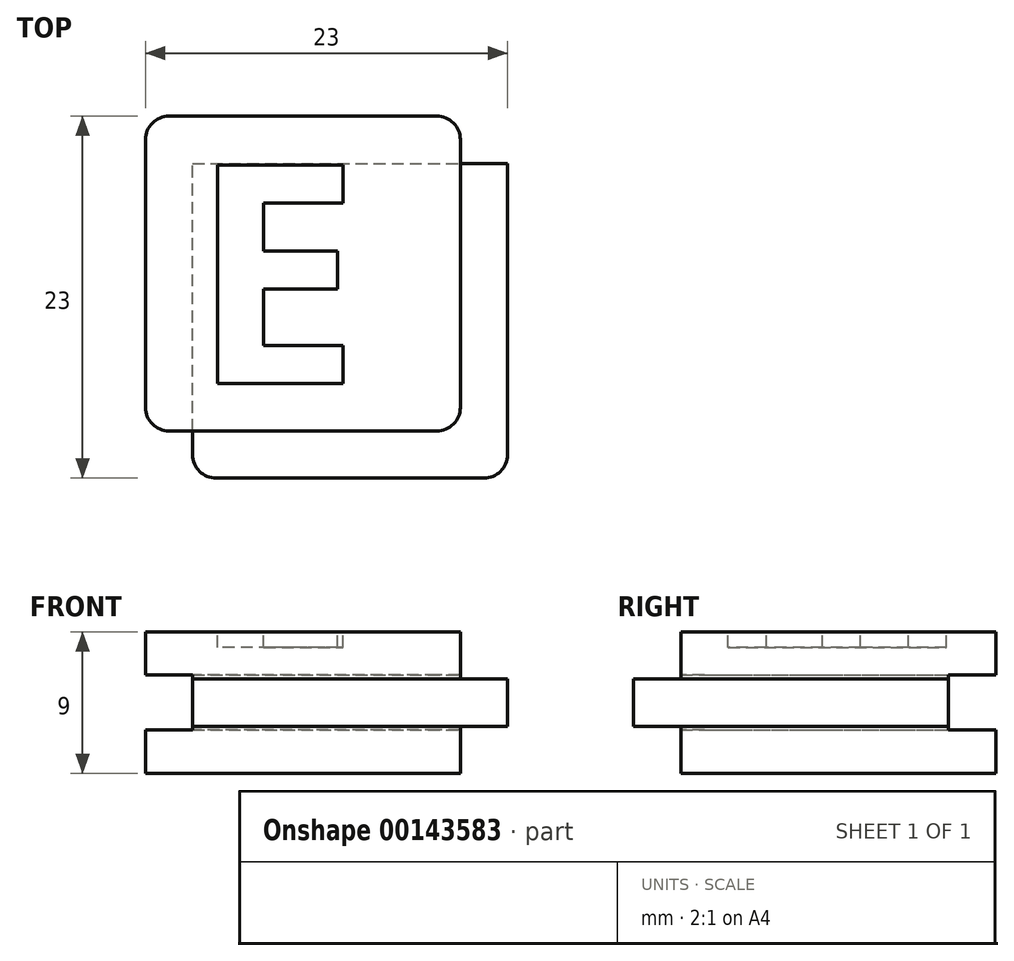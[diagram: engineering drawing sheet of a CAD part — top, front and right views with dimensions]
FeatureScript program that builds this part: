
annotation { "Feature Type Name" : "Feature", "Feature Type Description" : "" }
export const myFeature = defineFeature(function(context is Context, id is Id, definition is map)
    precondition{}
    {
        {
            var Q0;
            Q0=qCreatedBy(makeId("Front.planeOp"),FACE);
            var sketch = newSketch(context, id + "F0", { "sketchPlane" : qUnion([Q0])});
            skLineSegment(sketch, "E0.bottom", {"start": v(10, 4.5) * mm, "end": v(-10, 4.5) * mm});
            skLineSegment(sketch, "E0.top", {"start": v(10, -4.5) * mm, "end": v(-10, -4.5) * mm});
            skLineSegment(sketch, "E0.left", {"start": v(10, 4.5) * mm, "end": v(10, -4.5) * mm});
            skLineSegment(sketch, "E0.right", {"start": v(-10, 4.5) * mm, "end": v(-10, -4.5) * mm});
            skPoint(sketch, "E0.middle", {"position": v(0, 0) * mm});
            skLineSegment(sketch, "E1.bottom", {"start": v(13, 1.5) * mm, "end": v(7, 1.5) * mm});
            skLineSegment(sketch, "E1.top", {"start": v(13, -1.5) * mm, "end": v(7, -1.5) * mm});
            skLineSegment(sketch, "E1.left", {"start": v(13, 1.5) * mm, "end": v(13, -1.5) * mm});
            skLineSegment(sketch, "E1.right", {"start": v(7, 1.5) * mm, "end": v(7, -1.5) * mm});
            skPoint(sketch, "E1.middle", {"position": v(10, 0) * mm});
            skLineSegment(sketch, "E2.bottom", {"start": v(7, 1.5) * mm, "end": v(-7, 1.5) * mm});
            skLineSegment(sketch, "E2.top", {"start": v(7, -1.5) * mm, "end": v(-7, -1.5) * mm});
            skLineSegment(sketch, "E2.right", {"start": v(-7, 1.5) * mm, "end": v(-7, -1.5) * mm});
            skLineSegment(sketch, "E3.bottom", {"start": v(-7, -1.5) * mm, "end": v(-10, -1.5) * mm});
            skLineSegment(sketch, "E3.top", {"start": v(-7, 1.5) * mm, "end": v(-10, 1.5) * mm});
            skLineSegment(sketch, "E3.left", {"start": v(-7, -1.5) * mm, "end": v(-7, 1.5) * mm});
            skLineSegment(sketch, "E3.right", {"start": v(-10, -1.5) * mm, "end": v(-10, 1.5) * mm});
            skSolve(sketch);
        }
        {
            var Q0;
            {var subQ5=sQuery(id+"F0.wireOp",EDGE,"E0.bottom");Q0=makeQuery(id+"F0.imprint","IMPRINT",FACE,{"disambiguationData":[TD([[makeQuery(id+"F0.imprint","IMPRINT",EDGE,{"derivedFrom":subQ5}),1.0]])]});}
            var Q1;
            Q1=makeQuery(id+"F0.imprint","IMPRINT",FACE,{"disambiguationData":[TD([[makeQuery(id+"F0.imprint","IMPRINT",EDGE,{"derivedFrom":sQuery(id+"F0.wireOp",EDGE,"E2.bottom")}),1.0]])]});
            var Q2;
            {var subQ5=sQuery(id+"F0.wireOp",EDGE,"E1.left");Q2=makeQuery(id+"F0.imprint","IMPRINT",FACE,{"disambiguationData":[TD([[makeQuery(id+"F0.imprint","IMPRINT",EDGE,{"derivedFrom":subQ5}),-1.0]])]});}
            var Q3;
            {var subQ5=sQuery(id+"F0.wireOp",EDGE,"E1.right");Q3=makeQuery(id+"F0.imprint","IMPRINT",FACE,{"disambiguationData":[TD([[makeQuery(id+"F0.imprint","IMPRINT",EDGE,{"derivedFrom":subQ5}),1.0]])]});}
            var Q4;
            Q4=makeQuery(id+"F0.imprint","IMPRINT",FACE,{"disambiguationData":[TD([[makeQuery(id+"F0.imprint","IMPRINT",EDGE,{"derivedFrom":sQuery(id+"F0.wireOp",EDGE,"E3.bottom")}),-1.0]])]});
            var Q5;
            {var subQ5=sQuery(id+"F0.wireOp",EDGE,"E0.top");Q5=makeQuery(id+"F0.imprint","IMPRINT",FACE,{"disambiguationData":[TD([[makeQuery(id+"F0.imprint","IMPRINT",EDGE,{"derivedFrom":subQ5}),-1.0]])]});}
            extrude(context, id + "F1", {"entities" : qUnion([Q0, Q1, Q2, Q3, Q4, Q5]), "oppositeDirection" : true, "depth" : 20 * mm});
        }
        {
            var Q0;
            Q0=makeQuery(id+"F0.imprint","IMPRINT",FACE,{"disambiguationData":[TD([[makeQuery(id+"F0.imprint","IMPRINT",EDGE,{"derivedFrom":sQuery(id+"F0.wireOp",EDGE,"E3.bottom")}),-1.0]])]});
            var Q1;
            Q1=makeQuery(id+"F0.imprint","IMPRINT",FACE,{"disambiguationData":[TD([[makeQuery(id+"F0.imprint","IMPRINT",EDGE,{"derivedFrom":sQuery(id+"F0.wireOp",EDGE,"E2.bottom")}),1.0]])]});
            var Q2;
            {var subQ5=sQuery(id+"F0.wireOp",EDGE,"E1.right");Q2=makeQuery(id+"F0.imprint","IMPRINT",FACE,{"disambiguationData":[TD([[makeQuery(id+"F0.imprint","IMPRINT",EDGE,{"derivedFrom":subQ5}),1.0]])]});}
            var Q3;
            {var subQ5=sQuery(id+"F0.wireOp",EDGE,"E1.left");Q3=makeQuery(id+"F0.imprint","IMPRINT",FACE,{"disambiguationData":[TD([[makeQuery(id+"F0.imprint","IMPRINT",EDGE,{"derivedFrom":subQ5}),-1.0]])]});}
            extrude(context, id + "F2", {"entities" : qUnion([Q0, Q1, Q2, Q3]), "operationType" : NewBodyOperationType.ADD, "depth" : 3 * mm});
        }
        {
            var Q0;
            {var subQ0=sQuery(id+"F0.wireOp",EDGE,"E1.left");Q0=makeQuery(id+"F2.boolean.opBoolean","MERGE",FACE,{"derivedFrom":[makeQuery(id+"F1.opExtrude","SWEPT_FACE",FACE,{"disambiguationData":[OSD([subQ0])]}),makeQuery(id+"F2.opExtrude","SWEPT_FACE",FACE,{"disambiguationData":[OSD([subQ0])]})]});}
            var sketch = newSketch(context, id + "F3", { "sketchPlane" : qUnion([Q0])});
            skLineSegment(sketch, "E4.bottom", {"start": v(23, 1.75) * mm, "end": v(17, 1.75) * mm});
            skLineSegment(sketch, "E4.top", {"start": v(23, -1.75) * mm, "end": v(17, -1.75) * mm});
            skLineSegment(sketch, "E4.left", {"start": v(23, 1.75) * mm, "end": v(23, -1.75) * mm});
            skLineSegment(sketch, "E4.right", {"start": v(17, 1.75) * mm, "end": v(17, -1.75) * mm});
            skPoint(sketch, "E4.middle", {"position": v(20, 0) * mm});
            skSolve(sketch);
        }
        {
            var Q0;
            {var subQ1=sQuery(id+"F3.wireOp",EDGE,"E4.bottom");Q0=makeQuery(id+"F3.imprint","IMPRINT",FACE,{"disambiguationData":[TD([[makeQuery(id+"F3.imprint","IMPRINT",EDGE,{"derivedFrom":subQ1}),1.0]])]});}
            var Q1;
            {var subQ1=sQuery(id+"F0.wireOp",EDGE,"E1.left");var subQ8=makeQuery(id+"F1.opExtrude","CAP_EDGE",EDGE,{"disambiguationData":[OSD([subQ1])],"isStart":false});Q1=makeQuery(id+"F3.imprint","IMPRINT",FACE,{"disambiguationData":[TD([[makeQuery(id+"F3.imprint","IMPRINT",EDGE,{"derivedFrom":subQ8}),-1.0]])]});}
            extrude(context, id + "F4", {"entities" : qUnion([Q0, Q1]), "operationType" : NewBodyOperationType.REMOVE, "oppositeDirection" : true, "depth" : 100 * mm});
        }
        {
            var Q0;
            Q0=makeQuery(id+"F4.boolean.opBoolean","COPY",FACE,{"derivedFrom":makeQuery(id+"F4.opExtrude","SWEPT_FACE",FACE,{"disambiguationData":[OSD([sQuery(id+"F3.wireOp",EDGE,"E4.right")])]})});
            var sketch = newSketch(context, id + "F5", { "sketchPlane" : qUnion([Q0])});
            skLineSegment(sketch, "E5.bottom", {"start": v(13, 1.75) * mm, "end": v(7, 1.75) * mm});
            skLineSegment(sketch, "E5.top", {"start": v(13, -1.75) * mm, "end": v(7, -1.75) * mm});
            skLineSegment(sketch, "E5.left", {"start": v(13, 1.75) * mm, "end": v(13, -1.75) * mm});
            skLineSegment(sketch, "E5.right", {"start": v(7, 1.75) * mm, "end": v(7, -1.75) * mm});
            skPoint(sketch, "E5.middle", {"position": v(10, 0) * mm});
            skSolve(sketch);
        }
        {
            var Q0;
            {var subQ3=sQuery(id+"F5.wireOp",EDGE,"E5.left");Q0=makeQuery(id+"F5.imprint","IMPRINT",FACE,{"disambiguationData":[TD([[makeQuery(id+"F5.imprint","IMPRINT",EDGE,{"derivedFrom":subQ3}),-1.0]])]});}
            var Q1;
            {var subQ4=sQuery(id+"F5.wireOp",EDGE,"E5.right");Q1=makeQuery(id+"F5.imprint","IMPRINT",FACE,{"disambiguationData":[TD([[makeQuery(id+"F5.imprint","IMPRINT",EDGE,{"derivedFrom":subQ4}),1.0]])]});}
            extrude(context, id + "F6", {"entities" : qUnion([Q0, Q1]), "operationType" : NewBodyOperationType.REMOVE, "oppositeDirection" : true, "depth" : 100 * mm});
        }
        {
            var Q0;
            Q0=makeQuery(id+"F6.boolean.opBoolean","INTERSECT",EDGE,{"derivedFrom":[makeQuery(id+"F2.opExtrude","CAP_FACE",FACE,{"disambiguationData":[OSD([sQuery(id+"F0.wireOp",EDGE,"E1.bottom"),sQuery(id+"F0.wireOp",EDGE,"E1.top"),sQuery(id+"F0.wireOp",EDGE,"E1.left"),sQuery(id+"F0.wireOp",EDGE,"E2.bottom"),sQuery(id+"F0.wireOp",EDGE,"E2.top"),sQuery(id+"F0.wireOp",EDGE,"E3.bottom"),sQuery(id+"F0.wireOp",EDGE,"E3.top"),sQuery(id+"F0.wireOp",EDGE,"E3.right")])],"isStart":false}),makeQuery(id+"F6.opExtrude","SWEPT_FACE",FACE,{"disambiguationData":[OSD([sQuery(id+"F5.wireOp",EDGE,"E5.right")])]})]});
            var Q1;
            Q1=makeQuery(id+"F2.opExtrude","CAP_EDGE",EDGE,{"disambiguationData":[OSD([sQuery(id+"F0.wireOp",EDGE,"E1.left")])],"isStart":false});
            var Q2;
            {var subQ0=sQuery(id+"F0.wireOp",EDGE,"E0.left");Q2=makeQuery(id+"F1.opExtrude","CAP_EDGE",EDGE,{"disambiguationData":[OSD([subQ0]),TDD([makeQuery(id+"F0.imprint","IMPRINT",EDGE,{"disambiguationData":[TD([[makeQuery(id+"F0.imprint","INTERSECT",VERTEX,{"derivedFrom":[sQuery(id+"F0.wireOp",EDGE,"E0.bottom"),subQ0]}),-1.0]])],"derivedFrom":subQ0})])],"isStart":true});}
            var Q3;
            {var subQ0=sQuery(id+"F0.wireOp",EDGE,"E0.left");Q3=makeQuery(id+"F1.opExtrude","CAP_EDGE",EDGE,{"disambiguationData":[OSD([subQ0]),TDD([makeQuery(id+"F0.imprint","IMPRINT",EDGE,{"disambiguationData":[TD([[makeQuery(id+"F0.imprint","INTERSECT",VERTEX,{"derivedFrom":[sQuery(id+"F0.wireOp",EDGE,"E0.top"),subQ0]}),1.0]])],"derivedFrom":subQ0})])],"isStart":true});}
            var Q4;
            {var subQ0=sQuery(id+"F0.wireOp",EDGE,"E3.right");var subQ1=sQuery(id+"F0.wireOp",EDGE,"E0.right");var subQ3=sQuery(id+"F0.wireOp",EDGE,"E0.top");Q4=makeQuery(id+"F2.boolean.opBoolean","SPLIT",EDGE,{"disambiguationData":[TD([makeQuery(id+"F1.opExtrude","SWEPT_FACE",FACE,{"disambiguationData":[OSD([subQ3])]})])],"derivedFrom":makeQuery(id+"F1.opExtrude","CAP_EDGE",EDGE,{"disambiguationData":[OSD([subQ1,subQ0])],"isStart":true})});}
            var Q5;
            {var subQ1=sQuery(id+"F0.wireOp",EDGE,"E3.right");var subQ2=sQuery(id+"F0.wireOp",EDGE,"E0.right");var subQ3=sQuery(id+"F0.wireOp",EDGE,"E0.bottom");Q5=makeQuery(id+"F2.boolean.opBoolean","SPLIT",EDGE,{"disambiguationData":[TD([makeQuery(id+"F1.opExtrude","SWEPT_FACE",FACE,{"disambiguationData":[OSD([subQ3])]})])],"derivedFrom":makeQuery(id+"F1.opExtrude","CAP_EDGE",EDGE,{"disambiguationData":[OSD([subQ2,subQ1])],"isStart":true})});}
            var Q6;
            Q6=makeQuery(id+"F6.boolean.opBoolean","COPY",EDGE,{"derivedFrom":makeQuery(id+"F6.opExtrude","CAP_EDGE",EDGE,{"disambiguationData":[OSD([sQuery(id+"F5.wireOp",EDGE,"E5.right")])],"isStart":true})});
            var Q7;
            {var subQ0=sQuery(id+"F0.wireOp",EDGE,"E3.right");var subQ1=sQuery(id+"F0.wireOp",EDGE,"E0.right");var subQ2=sQuery(id+"F0.wireOp",EDGE,"E0.bottom");Q7=makeQuery(id+"F4.boolean.opBoolean","SPLIT",EDGE,{"disambiguationData":[TD([makeQuery(id+"F1.opExtrude","SWEPT_FACE",FACE,{"disambiguationData":[OSD([subQ2])]})])],"derivedFrom":makeQuery(id+"F1.opExtrude","CAP_EDGE",EDGE,{"disambiguationData":[OSD([subQ1,subQ0])],"isStart":false})});}
            var Q8;
            {var subQ0=sQuery(id+"F0.wireOp",EDGE,"E3.right");var subQ1=sQuery(id+"F0.wireOp",EDGE,"E0.right");var subQ2=sQuery(id+"F0.wireOp",EDGE,"E0.top");Q8=makeQuery(id+"F4.boolean.opBoolean","SPLIT",EDGE,{"disambiguationData":[TD([makeQuery(id+"F1.opExtrude","SWEPT_FACE",FACE,{"disambiguationData":[OSD([subQ2])]})])],"derivedFrom":makeQuery(id+"F1.opExtrude","CAP_EDGE",EDGE,{"disambiguationData":[OSD([subQ1,subQ0])],"isStart":false})});}
            var Q9;
            Q9=makeQuery(id+"F4.boolean.opBoolean","COPY",EDGE,{"derivedFrom":makeQuery(id+"F4.opExtrude","CAP_EDGE",EDGE,{"disambiguationData":[OSD([sQuery(id+"F3.wireOp",EDGE,"E4.right")])],"isStart":true})});
            var Q10;
            {var subQ0=sQuery(id+"F0.wireOp",EDGE,"E0.left");Q10=makeQuery(id+"F1.opExtrude","CAP_EDGE",EDGE,{"disambiguationData":[OSD([subQ0]),TDD([makeQuery(id+"F0.imprint","IMPRINT",EDGE,{"disambiguationData":[TD([[makeQuery(id+"F0.imprint","INTERSECT",VERTEX,{"derivedFrom":[sQuery(id+"F0.wireOp",EDGE,"E0.bottom"),subQ0]}),-1.0]])],"derivedFrom":subQ0})])],"isStart":false});}
            var Q11;
            {var subQ0=sQuery(id+"F0.wireOp",EDGE,"E0.left");Q11=makeQuery(id+"F1.opExtrude","CAP_EDGE",EDGE,{"disambiguationData":[OSD([subQ0]),TDD([makeQuery(id+"F0.imprint","IMPRINT",EDGE,{"disambiguationData":[TD([[makeQuery(id+"F0.imprint","INTERSECT",VERTEX,{"derivedFrom":[sQuery(id+"F0.wireOp",EDGE,"E0.top"),subQ0]}),1.0]])],"derivedFrom":subQ0})])],"isStart":false});}
            fillet(context, id + "F7", {"entities" : qUnion([Q0, Q1, Q2, Q3, Q4, Q5, Q6, Q7, Q8, Q9, Q10, Q11]), "radius" : 1.5 * mm, "tangentPropagation" : true, "allowEdgeOverflow" : false});
        }
        {
            var Q0;
            Q0=makeQuery(id+"F1.opExtrude","SWEPT_FACE",FACE,{"disambiguationData":[OSD([sQuery(id+"F0.wireOp",EDGE,"E0.bottom")])]});
            var sketch = newSketch(context, id + "F8", { "sketchPlane" : qUnion([Q0])});
            skText(sketch, "E6", { "text": "E", "fontName": "OpenSans-Bold.ttf"});
            skLineSegment(sketch, "E7.0", {"start": v(7.7, 3) * mm, "end": v(-11.07, 3) * mm});
            const initialGuessF8  = {"E6": [-0.00718, 0.003, 1, 0, 0.014]};
            skSetInitialGuess(sketch, initialGuessF8);
            skSolve(sketch);
        }
        {
            var Q0;
            {var subQ0=sQuery(id+"F8.wireOp",EDGE,"E6.sketch_text.stroke-1");Q0=makeQuery(id+"F8.imprint","IMPRINT",FACE,{"disambiguationData":[TD([[makeQuery(id+"F8.imprint","IMPRINT",EDGE,{"derivedFrom":subQ0}),-1.0]])]});}
            extrude(context, id + "F9", {"entities" : qUnion([Q0]), "operationType" : NewBodyOperationType.REMOVE, "oppositeDirection" : true, "depth" : 1 * mm});
        }
    });
